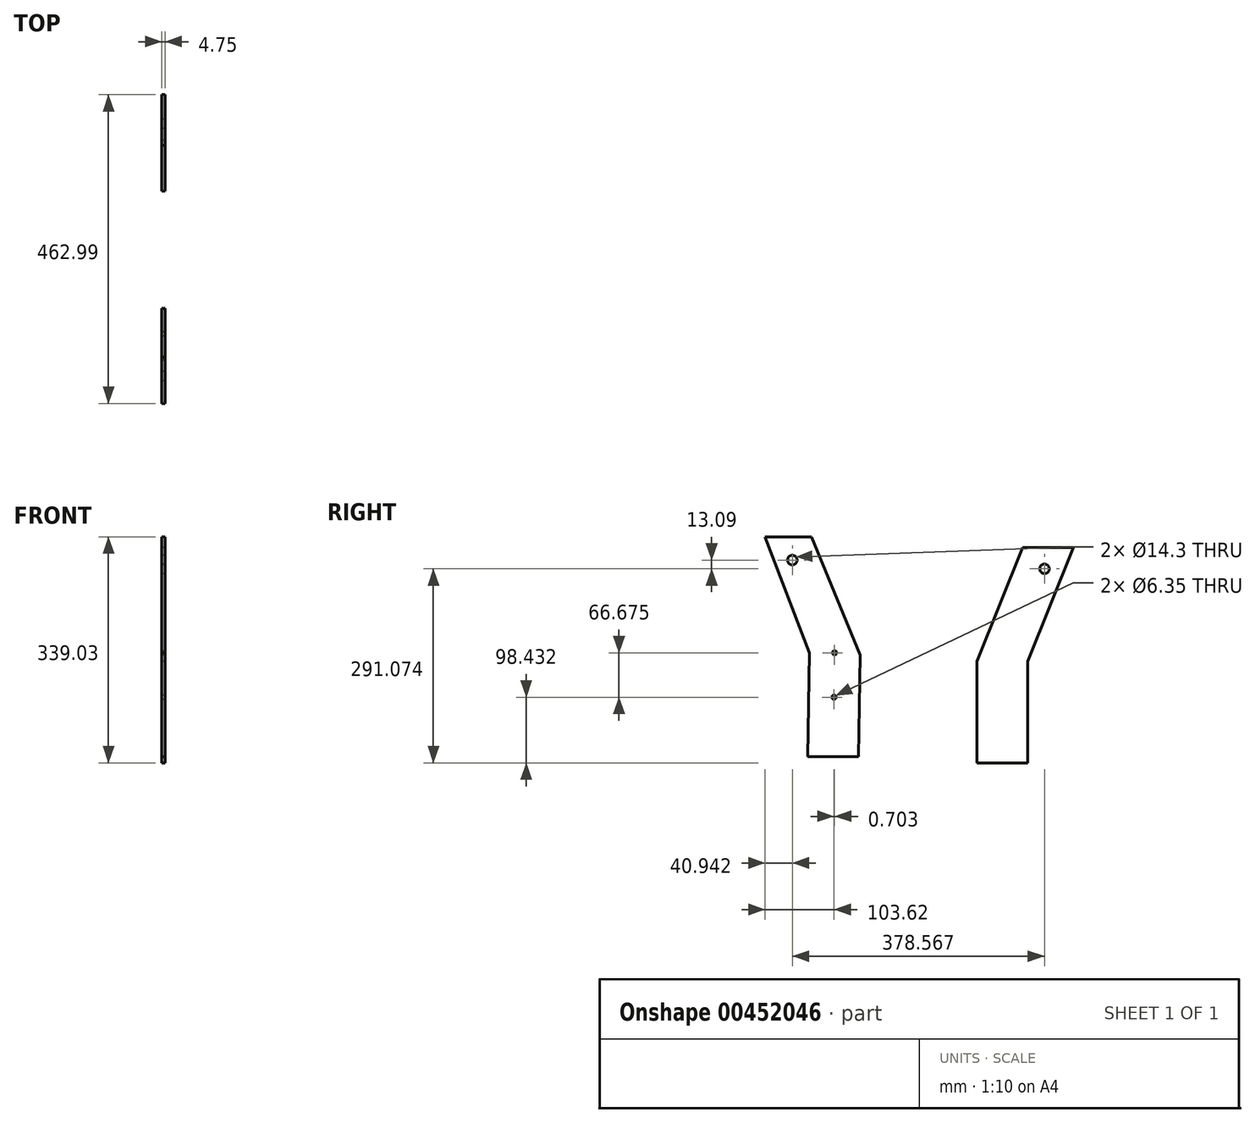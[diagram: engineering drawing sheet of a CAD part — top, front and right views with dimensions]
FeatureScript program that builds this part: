
annotation { "Feature Type Name" : "Feature", "Feature Type Description" : "" }
export const myFeature = defineFeature(function(context is Context, id is Id, definition is map)
    precondition{}
    {
        {
            var Q0;
            Q0=qCreatedBy(makeId("Right.planeOp"),FACE);
            var sketch = newSketch(context, id + "F0", { "sketchPlane" : qUnion([Q0])});
            skLineSegment(sketch, "E0.bottom", {"start": v(38.1, -165.1) * mm, "end": v(-38.1, -165.1) * mm});
            skPoint(sketch, "E0.middle", {"position": v(0, 0) * mm});
            skLineSegment(sketch, "E1", {"start": v(-38.1, -165.1) * mm, "end": v(-38.1, -12.7) * mm});
            skLineSegment(sketch, "E2", {"start": v(38.1, -165.1) * mm, "end": v(38.1, -12.7) * mm});
            skCircle(sketch, "E3", {"center": v(63.08, 125.97) * mm, "radius": 7.15 * mm});
            skLineSegment(sketch, "E4", {"start": v(-38.1, -12.7) * mm, "end": v(30.36, 157.72) * mm});
            skLineSegment(sketch, "E5", {"start": v(30.36, 157.72) * mm, "end": v(106.56, 157.72) * mm});
            skLineSegment(sketch, "E6", {"start": v(106.56, 157.72) * mm, "end": v(38.1, -12.7) * mm});
            skLineSegment(sketch, "E7.MirrorCS", {"start": v(-215.86, -155.57) * mm, "end": v(-292.06, -155.57) * mm});
            skCircle(sketch, "E8.MirrorC", {"center": v(-315.49, 139.06) * mm, "radius": 7.15 * mm});
            skLineSegment(sketch, "E9", {"start": v(-213.89, -3.17) * mm, "end": v(-286.58, 173.93) * mm});
            skLineSegment(sketch, "E10", {"start": v(-286.58, 173.93) * mm, "end": v(-356.43, 173.93) * mm});
            skLineSegment(sketch, "E11", {"start": v(-356.43, 173.93) * mm, "end": v(-290.09, 0) * mm});
            skLineSegment(sketch, "E12", {"start": v(-213.89, -3.17) * mm, "end": v(-215.86, -155.57) * mm});
            skCircle(sketch, "E13", {"center": v(-252.81, -66.67) * mm, "radius": 3.18 * mm});
            skCircle(sketch, "E14", {"center": v(-252.1, 0) * mm, "radius": 3.18 * mm});
            skLineSegment(sketch, "E15", {"start": v(-290.09, 0) * mm, "end": v(-292.06, -155.57) * mm});
            skSolve(sketch);
        }
        {
            var Q0;
            Q0=makeQuery(id+"F0.imprint","IMPRINT",FACE,{"disambiguationData":[TD([[makeQuery(id+"F0.imprint","IMPRINT",EDGE,{"derivedFrom":sQuery(id+"F0.wireOp",EDGE,"E0.bottom")}),-1.0]])]});
            var Q1;
            Q1=makeQuery(id+"F0.imprint","IMPRINT",FACE,{"disambiguationData":[TD([[makeQuery(id+"F0.imprint","IMPRINT",EDGE,{"derivedFrom":sQuery(id+"F0.wireOp",EDGE,"E7.MirrorCS")}),-1.0]])]});
            extrude(context, id + "F1", {"entities" : qUnion([Q0, Q1]), "depth" : 4.75 * mm});
        }
    });
